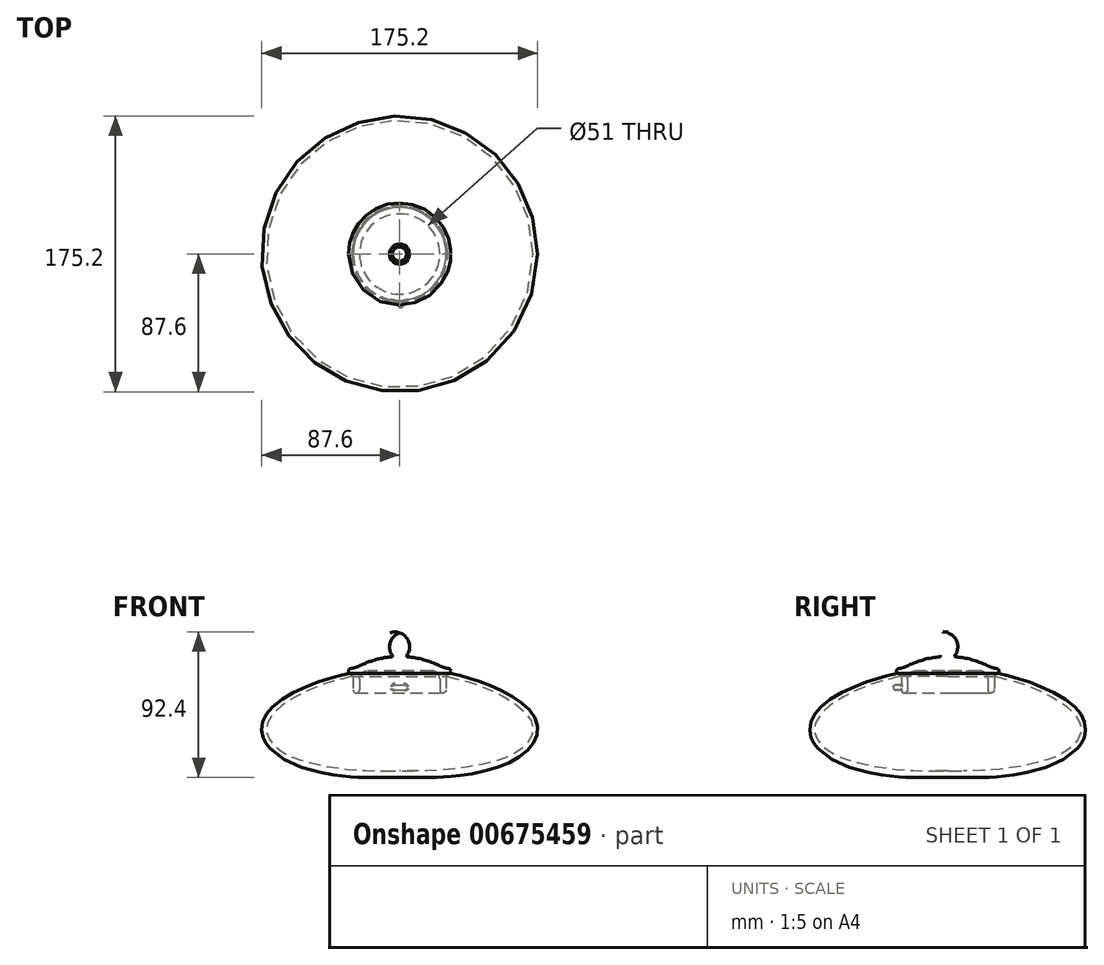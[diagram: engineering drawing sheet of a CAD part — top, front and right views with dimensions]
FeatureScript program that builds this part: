
annotation { "Feature Type Name" : "Feature", "Feature Type Description" : "" }
export const myFeature = defineFeature(function(context is Context, id is Id, definition is map)
    precondition{}
    {
        {
            var Q0;
            Q0=qCreatedBy(makeId("Front.planeOp"),FACE);
            var sketch = newSketch(context, id + "F0", { "sketchPlane" : qUnion([Q0])});
            skLineSegment(sketch, "E0", {"start": v(0, 0) * mm, "end": v(0, 9.24) * mm, "construction": true});
            skArc(sketch, "E1", {"start": v(0, 9.24) * mm, "mid": v(-16.17, 6.88) * mm, "end": v(-31, 0) * mm});
            skCircle(sketch, "E2", {"center": v(-31, 0) * mm, "radius": 1.5 * mm});
            skLineSegment(sketch, "E3", {"start": v(-31, 0) * mm, "end": v(-31, -1.5) * mm, "construction": true});
            skLineSegment(sketch, "E4", {"start": v(-31, 0) * mm, "end": v(-29.5, 0) * mm, "construction": true});
            skPoint(sketch, "E5", {"position": v(0, 5.24) * mm});
            skLineSegment(sketch, "E6", {"start": v(0, 5.24) * mm, "end": v(0, 9.24) * mm});
            skLineSegment(sketch, "E7.bottom", {"start": v(-29.5, 0) * mm, "end": v(-25.5, 0) * mm});
            skLineSegment(sketch, "E7.top", {"start": v(-29.5, -12) * mm, "end": v(-25.5, -12) * mm});
            skLineSegment(sketch, "E7.left", {"start": v(-29.5, 0) * mm, "end": v(-29.5, -12) * mm});
            skLineSegment(sketch, "E7.right", {"start": v(-25.5, 0) * mm, "end": v(-25.5, -12) * mm});
            skLineSegment(sketch, "E8", {"start": v(-25.5, 0) * mm, "end": v(0, 0) * mm});
            skLineSegment(sketch, "E9", {"start": v(0, 5.24) * mm, "end": v(0, 0) * mm});
            skPoint(sketch, "E10", {"position": v(-27.5, -12) * mm});
            skArc(sketch, "E11", {"start": v(-29.5, -12) * mm, "mid": v(-27.5, -14) * mm, "end": v(-25.5, -12) * mm});
            skPoint(sketch, "E12", {"position": v(0, 6.37) * mm});
            skPoint(sketch, "E13", {"position": v(0, 24.24) * mm});
            skArc(sketch, "E14", {"start": v(0, 24.24) * mm, "mid": v(-6.38, 15.3) * mm, "end": v(0, 6.37) * mm});
            skLineSegment(sketch, "E15", {"start": v(0, 9.24) * mm, "end": v(0, 24.24) * mm});
            skSolve(sketch);
        }
        {
            var Q0;
            {var subQ0=sQuery(id+"F0.wireOp",EDGE,"lw74teHP-5U6m-3WXN-i8PT-7hJfMxpOBeKC");Q0=makeQuery(id+"F0.imprint","IMPRINT",FACE,{"disambiguationData":[TD([[makeQuery(id+"F0.imprint","IMPRINT",EDGE,{"derivedFrom":subQ0}),1.0]])]});}
            var Q1;
            {var subQ0=sQuery(id+"F0.wireOp",EDGE,"E2");var subQ1=makeQuery(id+"F0.imprint","INTERSECT",VERTEX,{"derivedFrom":[subQ0,sQuery(id+"F0.wireOp",EDGE,"ZzognFwH-Ojfa-i7V0-dFbg-w2fNcsdz0ufx")]});Q1=makeQuery(id+"F0.imprint","IMPRINT",FACE,{"disambiguationData":[TD([[makeQuery(id+"F0.imprint","IMPRINT",EDGE,{"disambiguationData":[TD([[subQ1,1.0]])],"derivedFrom":subQ0}),1.0]])]});}
            var Q2;
            Q2=makeQuery(id+"F0.imprint","IMPRINT",FACE,{"disambiguationData":[TD([[makeQuery(id+"F0.imprint","IMPRINT",EDGE,{"derivedFrom":sQuery(id+"F0.wireOp",EDGE,"gq6tdRw2-1AHc-x8Jy-w9v6-sO9QvOB3eNEJ.top")}),-1.0]])]});
            var Q3;
            {var subQ0=sQuery(id+"F0.wireOp",EDGE,"E6");var subQ3=sQuery(id+"F0.wireOp",EDGE,"v3pWdLWY-bHeT-sS10-8cdN-XUToxixwMHi3");var subQ5=makeQuery(id+"F0.imprint","INTERSECT",VERTEX,{"derivedFrom":[subQ0,subQ3]});Q3=makeQuery(id+"F0.imprint","IMPRINT",FACE,{"disambiguationData":[TD([[makeQuery(id+"F0.imprint","IMPRINT",EDGE,{"disambiguationData":[TD([[subQ5,1.0]])],"derivedFrom":subQ3}),1.0]])]});}
            var Q4;
            Q4=makeQuery(id+"F0.imprint","IMPRINT",FACE,{"disambiguationData":[TD([[makeQuery(id+"F0.imprint","IMPRINT",EDGE,{"derivedFrom":sQuery(id+"F0.wireOp",EDGE,"gq6tdRw2-1AHc-x8Jy-w9v6-sO9QvOB3eNEJ.bottom")}),-1.0]])]});
            var Q5;
            {var subQ0=sQuery(id+"F0.wireOp",EDGE,"ZzognFwH-Ojfa-i7V0-dFbg-w2fNcsdz0ufx");Q5=makeQuery(id+"F0.imprint","IMPRINT",FACE,{"disambiguationData":[TD([[makeQuery(id+"F0.imprint","IMPRINT",EDGE,{"derivedFrom":subQ0}),-1.0]])]});}
            var Q6;
            {var subQ6=sQuery(id+"F0.wireOp",EDGE,"E7.bottom");Q6=makeQuery(id+"F0.imprint","IMPRINT",FACE,{"disambiguationData":[TD([[makeQuery(id+"F0.imprint","IMPRINT",EDGE,{"derivedFrom":subQ6}),1.0]])]});}
            var Q7;
            Q7=makeQuery(id+"F0.imprint","IMPRINT",FACE,{"disambiguationData":[TD([[makeQuery(id+"F0.imprint","IMPRINT",EDGE,{"derivedFrom":sQuery(id+"F0.wireOp",EDGE,"E7.bottom")}),-1.0]])]});
            var Q8;
            Q8=makeQuery(id+"F0.imprint","IMPRINT",FACE,{"disambiguationData":[TD([[makeQuery(id+"F0.imprint","IMPRINT",EDGE,{"derivedFrom":sQuery(id+"F0.wireOp",EDGE,"E7.top")}),-1.0]])]});
            var Q9;
            {var subQ0=sQuery(id+"F0.wireOp",EDGE,"sZk0aHvy-GrzH-x6xV-Dy0i-avqQmov7gIlc");Q9=makeQuery(id+"F0.imprint","IMPRINT",FACE,{"disambiguationData":[TD([[makeQuery(id+"F0.imprint","IMPRINT",EDGE,{"derivedFrom":subQ0}),1.0]])]});}
            var Q10;
            {var subQ0=sQuery(id+"F0.wireOp",EDGE,"E6");var subQ3=sQuery(id+"F0.wireOp",EDGE,"HXm6clT2-WLKA-nYjc-tjND-AT0Z1uAqKyUc");var subQ5=makeQuery(id+"F0.imprint","INTERSECT",VERTEX,{"derivedFrom":[subQ0,subQ3]});Q10=makeQuery(id+"F0.imprint","IMPRINT",FACE,{"disambiguationData":[TD([[makeQuery(id+"F0.imprint","IMPRINT",EDGE,{"disambiguationData":[TD([[subQ5,1.0]])],"derivedFrom":subQ3}),1.0]])]});}
            var Q11;
            {var subQ0=sQuery(id+"F0.wireOp",EDGE,"E15");Q11=makeQuery(id+"F0.imprint","IMPRINT",FACE,{"disambiguationData":[TD([[makeQuery(id+"F0.imprint","IMPRINT",EDGE,{"derivedFrom":subQ0}),1.0]])]});}
            var Q12;
            {var subQ0=sQuery(id+"F0.wireOp",EDGE,"E6");var subQ3=sQuery(id+"F0.wireOp",EDGE,"E14");var subQ5=makeQuery(id+"F0.imprint","INTERSECT",VERTEX,{"derivedFrom":[subQ0,subQ3]});Q12=makeQuery(id+"F0.imprint","IMPRINT",FACE,{"disambiguationData":[TD([[makeQuery(id+"F0.imprint","IMPRINT",EDGE,{"disambiguationData":[TD([[subQ5,1.0]])],"derivedFrom":subQ3}),1.0]])]});}
            var Q13;
            Q13=sQuery(id+"F0.wireOp",EDGE,"E0");
            revolve(context, id + "F1", {"entities" : qUnion([Q0, Q1, Q2, Q3, Q4, Q5, Q6, Q7, Q8, Q9, Q10, Q11, Q12]), "axis" : qUnion([Q13]), "revolveType" : RevolveType.FULL});
        }
        {
            var Q0;
            Q0=makeQuery(id+"F1.opRevolve","SWEPT_FACE",FACE,{"disambiguationData":[OSD([sQuery(id+"F0.wireOp",EDGE,"E7.left")])]});
            fillet(context, id + "F2", {"entities" : qUnion([Q0]), "radius" : 2 * mm, "tangentPropagation" : true, "allowEdgeOverflow" : false});
        }
        {
            var Q0;
            Q0=makeQuery(id+"F1.opRevolve","SWEPT_EDGE",EDGE,{"disambiguationData":[OSD([sQuery(id+"F0.wireOp",EDGE,"E7.bottom"),sQuery(id+"F0.wireOp",EDGE,"E7.right"),sQuery(id+"F0.wireOp",EDGE,"E8")])]});
            fillet(context, id + "F3", {"entities" : qUnion([Q0]), "radius" : 5 * mm, "tangentPropagation" : true, "allowEdgeOverflow" : false});
        }
        {
            var Q0;
            Q0=makeQuery(id+"F1.opRevolve","SWEPT_EDGE",EDGE,{"disambiguationData":[OSD([sQuery(id+"F0.wireOp",EDGE,"E1"),sQuery(id+"F0.wireOp",EDGE,"E14")])]});
            fillet(context, id + "F4", {"entities" : qUnion([Q0]), "radius" : 0.5 * mm, "tangentPropagation" : true, "allowEdgeOverflow" : false});
        }
        {
            var Q0;
            Q0=makeQuery(id+"F1.opRevolve","SWEPT_EDGE",EDGE,{"disambiguationData":[OSD([sQuery(id+"F0.wireOp",EDGE,"E1"),sQuery(id+"F0.wireOp",EDGE,"E2")])]});
            fillet(context, id + "F5", {"entities" : qUnion([Q0]), "radius" : 20.74 * mm, "allowEdgeOverflow" : false});
        }
        {
            var Q0;
            Q0=qCreatedBy(makeId("Top.planeOp"),FACE);
            cPlane(context, id + "F6", {"entities" : qUnion([Q0]), "cplaneType" : CPlaneType.OFFSET, "offset" : 12 * mm, "oppositeDirection" : true, "width" : 150 * mm, "height" : 150 * mm});
        }
        {
            var Q0;
            Q0=qCreatedBy(id+"F6.planeOp",FACE);
            var sketch = newSketch(context, id + "F7", { "sketchPlane" : qUnion([Q0])});
            skLineSegment(sketch, "E16", {"start": v(0, 0) * mm, "end": v(0, -29.5) * mm, "construction": true});
            skCircle(sketch, "E17", {"center": v(0, 0) * mm, "radius": 29.5 * mm, "construction": true});
            skLineSegment(sketch, "E18", {"start": v(0, 0) * mm, "end": v(-5.12, -29.05) * mm, "construction": true});
            skLineSegment(sketch, "E19", {"start": v(0, 0) * mm, "end": v(5.12, -29.05) * mm, "construction": true});
            skLineSegment(sketch, "E20", {"start": v(0, -29.5) * mm, "end": v(0, -34.5) * mm, "construction": true});
            skFitSpline(sketch, "E21", {"points": [v(-5.12, -29.05) * mm, v(0, -34.5) * mm, v(5.12, -29.05) * mm], "startDerivative": vector(12.74, -17.69) * mm, "endDerivative": vector(12.74, 17.69) * mm});
            skPoint(sketch, "E22", {"position": v(0, -32) * mm});
            skArc(sketch, "E23", {"start": v(-5.12, -29.05) * mm, "mid": v(0, -29.5) * mm, "end": v(5.12, -29.05) * mm});
            skSolve(sketch);
        }
        {
            var Q0;
            Q0 = qSketchRegion(id + "F7", true);
            extrude(context, id + "F8", {"entities" : qUnion([Q0]), "operationType" : NewBodyOperationType.ADD, "depth" : 3 * mm, "offsetDistance" : 25 * mm});
        }
        {
            var Q0;
            Q0=makeQuery(id+"F1.opRevolve","SWEPT_FACE",FACE,{"disambiguationData":[OSD([sQuery(id+"F0.wireOp",EDGE,"E7.left")])]});
            var Q1;
            Q1=makeQuery(id+"F8.opExtrude","CAP_EDGE",EDGE,{"disambiguationData":[OSD([sQuery(id+"F7.wireOp",EDGE,"E21")])],"isStart":false});
            var Q2;
            Q2=makeQuery(id+"F8.boolean.opBoolean","MERGE",EDGE,{"derivedFrom":[makeQuery(id+"F1.opRevolve","SWEPT_EDGE",EDGE,{"disambiguationData":[OSD([sQuery(id+"F0.wireOp",EDGE,"E7.top"),sQuery(id+"F0.wireOp",EDGE,"E7.left"),sQuery(id+"F0.wireOp",EDGE,"E11")])]}),makeQuery(id+"F8.opExtrude","CAP_EDGE",EDGE,{"disambiguationData":[OSD([sQuery(id+"F7.wireOp",EDGE,"E23")])],"isStart":true})]});
            var Q3;
            Q3=makeQuery(id+"F8.opExtrude","CAP_EDGE",EDGE,{"disambiguationData":[OSD([sQuery(id+"F7.wireOp",EDGE,"E21")])],"isStart":true});
            fillet(context, id + "F9", {"entities" : qUnion([Q0, Q1, Q2, Q3]), "radius" : 1 * mm, "tangentPropagation" : true, "allowEdgeOverflow" : false});
        }
        {
            var Q0;
            Q0=qCreatedBy(makeId("Front.planeOp"),FACE);
            var sketch = newSketch(context, id + "F10", { "sketchPlane" : qUnion([Q0])});
            skLineSegment(sketch, "E24.0", {"start": v(29.5, -3.46) * mm, "end": v(-29.5, -3.46) * mm});
            skLineSegment(sketch, "E25", {"start": v(29.5, -3.46) * mm, "end": v(30.5, -3.46) * mm, "construction": true});
            skLineSegment(sketch, "E26.0", {"start": v(-31.21, -1.48) * mm, "end": v(31.21, -1.48) * mm});
            skLineSegment(sketch, "E27", {"start": v(31.21, -1.48) * mm, "end": v(32.21, -1.48) * mm, "construction": true});
            skArc(sketch, "E28", {"start": v(32.21, -1.48) * mm, "mid": v(30.9, -2.08) * mm, "end": v(30.5, -3.46) * mm});
            skFitSpline(sketch, "E29", {"points": [v(32.21, -1.48) * mm, v(57.24, -9.15) * mm, v(83.99, -26.57) * mm, v(86.26, -43.28) * mm, v(65.33, -60.15) * mm, v(32.21, -67.07) * mm, v(0, -67.63) * mm], "startDerivative": vector(146.09, -34.44) * mm, "endDerivative": vector(-387.27, 0) * mm});
            skFitSpline(sketch, "E30", {"points": [v(30.5, -3.46) * mm, v(35.72, -4.86) * mm, v(55.92, -11.33) * mm, v(80.8, -27.66) * mm, v(84.54, -39.48) * mm, v(78, -48.81) * mm, v(65.72, -55.66) * mm, v(32.59, -62.5) * mm, v(0, -63.43) * mm], "startDerivative": vector(65.77, -17.96) * mm, "endDerivative": vector(-190.73, 2.51) * mm});
            skLineSegment(sketch, "E31", {"start": v(0, -63.43) * mm, "end": v(0, -67.63) * mm});
            skLineSegment(sketch, "E32", {"start": v(0, -63.43) * mm, "end": v(0, -27.76) * mm, "construction": true});
            skSolve(sketch);
        }
        {
            var Q0;
            Q0 = qSketchRegion(id + "F10", true);
            var Q1;
            Q1=sQuery(id+"F10.wireOp",EDGE,"E32");
            revolve(context, id + "F11", {"surfaceOperationType" : NewSurfaceOperationType.NEW, "entities" : qUnion([Q0]), "axis" : qUnion([Q1]), "revolveType" : RevolveType.FULL});
        }
    });
